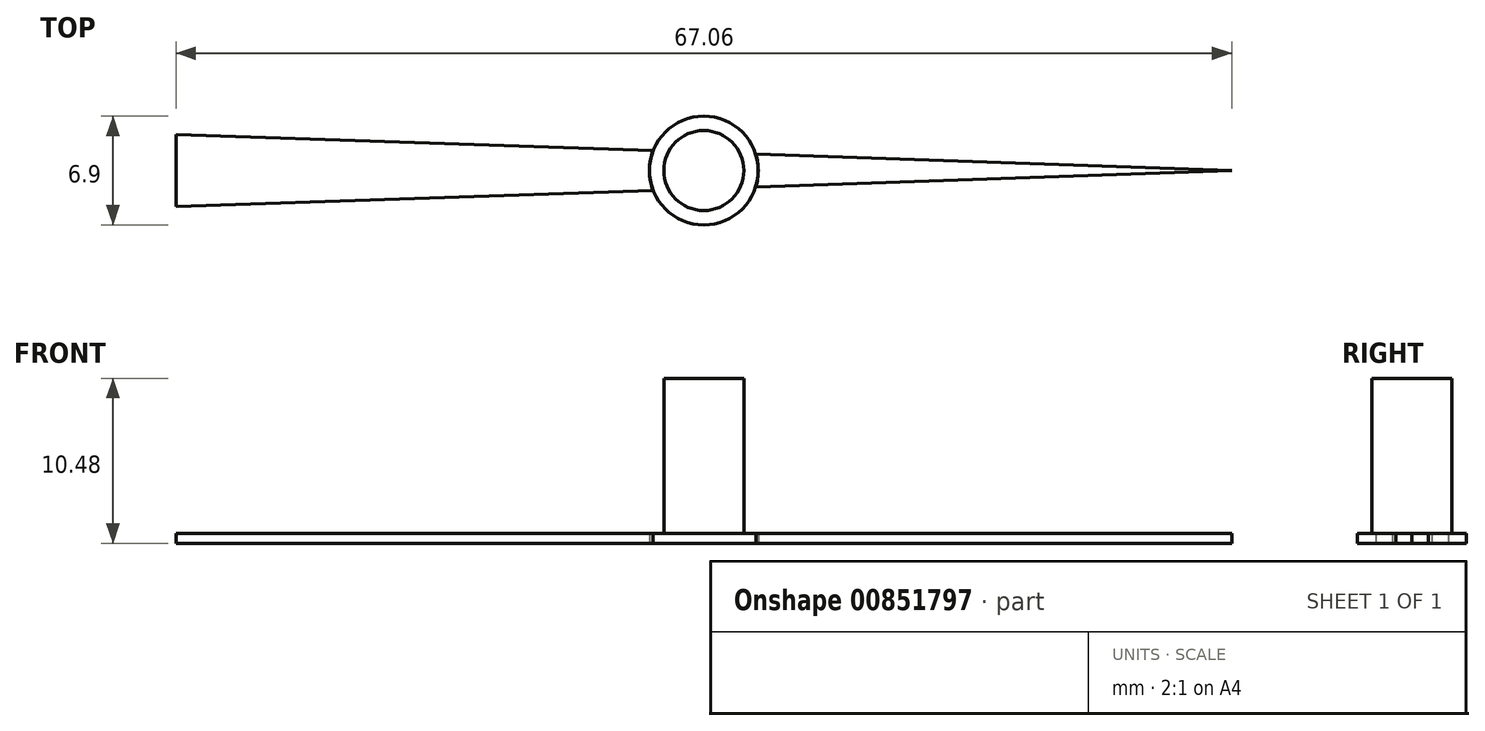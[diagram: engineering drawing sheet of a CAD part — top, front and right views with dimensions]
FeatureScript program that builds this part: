
annotation { "Feature Type Name" : "Feature", "Feature Type Description" : "" }
export const myFeature = defineFeature(function(context is Context, id is Id, definition is map)
    precondition{}
    {
        {
            var Q0;
            Q0=qCreatedBy(makeId("Top.planeOp"),FACE);
            var sketch = newSketch(context, id + "F0", { "sketchPlane" : qUnion([Q0])});
            skLineSegment(sketch, "E0.left", {"start": v(-33.53, 2.3) * mm, "end": v(-33.53, -2.3) * mm});
            skPoint(sketch, "E0.middle", {"position": v(0, 0) * mm});
            skPoint(sketch, "E1", {"position": v(33.53, 0) * mm});
            skLineSegment(sketch, "E2", {"start": v(33.53, 0) * mm, "end": v(-33.53, 2.3) * mm});
            skLineSegment(sketch, "E3", {"start": v(33.53, 0) * mm, "end": v(-33.53, -2.3) * mm});
            skCircle(sketch, "E4", {"center": v(0, 0) * mm, "radius": 3.45 * mm});
            skLineSegment(sketch, "E5.bottom", {"start": v(-2.67, 0.95) * mm, "end": v(2.67, 0.95) * mm});
            skLineSegment(sketch, "E5.top", {"start": v(-2.67, -0.95) * mm, "end": v(2.67, -0.95) * mm});
            skLineSegment(sketch, "E5.left", {"start": v(-2.67, 0.95) * mm, "end": v(-2.67, -0.95) * mm});
            skLineSegment(sketch, "E5.right", {"start": v(2.67, 0.95) * mm, "end": v(2.67, -0.95) * mm});
            skCircle(sketch, "E6", {"center": v(0, 0) * mm, "radius": 2.54 * mm});
            skCircle(sketch, "E7", {"center": v(0, 0) * mm, "radius": 3.46 * mm});
            skSolve(sketch);
        }
        {
            var Q0;
            {var subQ0=sQuery(id+"F0.wireOp",EDGE,"E0.left");Q0=makeQuery(id+"F0.imprint","IMPRINT",FACE,{"disambiguationData":[TD([[makeQuery(id+"F0.imprint","IMPRINT",EDGE,{"derivedFrom":subQ0}),1.0]])]});}
            var Q1;
            {var subQ0=sQuery(id+"F0.wireOp",EDGE,"E4");var subQ1=sQuery(id+"F0.wireOp",EDGE,"E3");var subQ2=makeQuery(id+"F0.imprint","INTERSECT",VERTEX,{"disambiguationData":[OD(0.0)],"derivedFrom":[subQ1,subQ0]});Q1=makeQuery(id+"F0.imprint","IMPRINT",FACE,{"disambiguationData":[TD([[makeQuery(id+"F0.imprint","IMPRINT",EDGE,{"disambiguationData":[TD([[subQ2,-1.0]])],"derivedFrom":subQ1}),1.0]])]});}
            var Q2;
            {var subQ0=sQuery(id+"F0.wireOp",EDGE,"E3");var subQ1=sQuery(id+"F0.wireOp",EDGE,"E2");var subQ2=makeQuery(id+"F0.imprint","INTERSECT",VERTEX,{"derivedFrom":[subQ1,subQ0]});Q2=makeQuery(id+"F0.imprint","IMPRINT",FACE,{"disambiguationData":[TD([[makeQuery(id+"F0.imprint","IMPRINT",EDGE,{"disambiguationData":[TD([[subQ2,-1.0]])],"derivedFrom":subQ1}),1.0]])]});}
            var Q3;
            {var subQ0=sQuery(id+"F0.wireOp",EDGE,"E4");var subQ1=sQuery(id+"F0.wireOp",EDGE,"E2");var subQ2=makeQuery(id+"F0.imprint","INTERSECT",VERTEX,{"disambiguationData":[OD(0.0)],"derivedFrom":[subQ1,subQ0]});Q3=makeQuery(id+"F0.imprint","IMPRINT",FACE,{"disambiguationData":[TD([[makeQuery(id+"F0.imprint","IMPRINT",EDGE,{"disambiguationData":[TD([[subQ2,-1.0]])],"derivedFrom":subQ1}),-1.0]])]});}
            var Q4;
            {var subQ0=sQuery(id+"F0.wireOp",EDGE,"E5.left");Q4=makeQuery(id+"F0.imprint","IMPRINT",FACE,{"disambiguationData":[TD([[makeQuery(id+"F0.imprint","IMPRINT",EDGE,{"derivedFrom":subQ0}),-1.0]])]});}
            var Q5;
            {var subQ5=sQuery(id+"F0.wireOp",EDGE,"E5.right");Q5=makeQuery(id+"F0.imprint","IMPRINT",FACE,{"disambiguationData":[TD([[makeQuery(id+"F0.imprint","IMPRINT",EDGE,{"derivedFrom":subQ5}),1.0]])]});}
            extrude(context, id + "F1", {"entities" : qUnion([Q0, Q1, Q2, Q3, Q4, Q5]), "endBound" : BoundingType.SYMMETRIC, "depth" : 0.64 * mm, "offsetDistance" : 25.4 * mm});
        }
        {
            var Q0;
            {var subQ0=sQuery(id+"F0.wireOp",EDGE,"E6");var subQ1=sQuery(id+"F0.wireOp",EDGE,"E3");var subQ2=makeQuery(id+"F0.imprint","INTERSECT",VERTEX,{"disambiguationData":[OD(0.0)],"derivedFrom":[subQ1,subQ0]});Q0=makeQuery(id+"F0.imprint","IMPRINT",FACE,{"disambiguationData":[TD([[makeQuery(id+"F0.imprint","IMPRINT",EDGE,{"disambiguationData":[TD([[subQ2,-1.0]])],"derivedFrom":subQ1}),1.0]])]});}
            var Q1;
            {var subQ0=sQuery(id+"F0.wireOp",EDGE,"E6");var subQ1=sQuery(id+"F0.wireOp",EDGE,"E2");var subQ2=makeQuery(id+"F0.imprint","INTERSECT",VERTEX,{"disambiguationData":[OD(0.0)],"derivedFrom":[subQ1,subQ0]});Q1=makeQuery(id+"F0.imprint","IMPRINT",FACE,{"disambiguationData":[TD([[makeQuery(id+"F0.imprint","IMPRINT",EDGE,{"disambiguationData":[TD([[subQ2,-1.0]])],"derivedFrom":subQ1}),-1.0]])]});}
            var Q2;
            {var subQ0=sQuery(id+"F0.wireOp",EDGE,"E6");var subQ1=sQuery(id+"F0.wireOp",EDGE,"E5.bottom");var subQ2=makeQuery(id+"F0.imprint","INTERSECT",VERTEX,{"disambiguationData":[OD(0.0)],"derivedFrom":[subQ1,subQ0]});Q2=makeQuery(id+"F0.imprint","IMPRINT",FACE,{"disambiguationData":[TD([[makeQuery(id+"F0.imprint","IMPRINT",EDGE,{"disambiguationData":[TD([[subQ2,-1.0]])],"derivedFrom":subQ1}),-1.0]])]});}
            var Q3;
            {var subQ0=sQuery(id+"F0.wireOp",EDGE,"E6");var subQ1=sQuery(id+"F0.wireOp",EDGE,"E2");var subQ2=makeQuery(id+"F0.imprint","INTERSECT",VERTEX,{"disambiguationData":[OD(0.0)],"derivedFrom":[subQ1,subQ0]});Q3=makeQuery(id+"F0.imprint","IMPRINT",FACE,{"disambiguationData":[TD([[makeQuery(id+"F0.imprint","IMPRINT",EDGE,{"disambiguationData":[TD([[subQ2,-1.0]])],"derivedFrom":subQ1}),1.0]])]});}
            var Q4;
            {var subQ0=sQuery(id+"F0.wireOp",EDGE,"E6");var subQ1=sQuery(id+"F0.wireOp",EDGE,"E3");var subQ2=makeQuery(id+"F0.imprint","INTERSECT",VERTEX,{"disambiguationData":[OD(0.0)],"derivedFrom":[subQ1,subQ0]});Q4=makeQuery(id+"F0.imprint","IMPRINT",FACE,{"disambiguationData":[TD([[makeQuery(id+"F0.imprint","IMPRINT",EDGE,{"disambiguationData":[TD([[subQ2,-1.0]])],"derivedFrom":subQ1}),-1.0]])]});}
            extrude(context, id + "F2", {"entities" : qUnion([Q0, Q1, Q2, Q3, Q4]), "operationType" : NewBodyOperationType.ADD, "depth" : 10.16 * mm, "offsetDistance" : 25.4 * mm});
        }
        {
            var Q0;
            {var subQ0=sQuery(id+"F0.wireOp",EDGE,"E6");var subQ1=sQuery(id+"F0.wireOp",EDGE,"E3");var subQ2=makeQuery(id+"F0.imprint","INTERSECT",VERTEX,{"disambiguationData":[OD(0.0)],"derivedFrom":[subQ1,subQ0]});Q0=makeQuery(id+"F0.imprint","IMPRINT",FACE,{"disambiguationData":[TD([[makeQuery(id+"F0.imprint","IMPRINT",EDGE,{"disambiguationData":[TD([[subQ2,-1.0]])],"derivedFrom":subQ1}),1.0]])]});}
            var Q1;
            {var subQ0=sQuery(id+"F0.wireOp",EDGE,"E6");var subQ1=sQuery(id+"F0.wireOp",EDGE,"E5.bottom");var subQ2=makeQuery(id+"F0.imprint","INTERSECT",VERTEX,{"disambiguationData":[OD(0.0)],"derivedFrom":[subQ1,subQ0]});Q1=makeQuery(id+"F0.imprint","IMPRINT",FACE,{"disambiguationData":[TD([[makeQuery(id+"F0.imprint","IMPRINT",EDGE,{"disambiguationData":[TD([[subQ2,-1.0]])],"derivedFrom":subQ1}),-1.0]])]});}
            var Q2;
            {var subQ0=sQuery(id+"F0.wireOp",EDGE,"E6");var subQ1=sQuery(id+"F0.wireOp",EDGE,"E2");var subQ2=makeQuery(id+"F0.imprint","INTERSECT",VERTEX,{"disambiguationData":[OD(0.0)],"derivedFrom":[subQ1,subQ0]});Q2=makeQuery(id+"F0.imprint","IMPRINT",FACE,{"disambiguationData":[TD([[makeQuery(id+"F0.imprint","IMPRINT",EDGE,{"disambiguationData":[TD([[subQ2,-1.0]])],"derivedFrom":subQ1}),-1.0]])]});}
            var Q3;
            {var subQ0=sQuery(id+"F0.wireOp",EDGE,"E6");var subQ1=sQuery(id+"F0.wireOp",EDGE,"E3");var subQ2=makeQuery(id+"F0.imprint","INTERSECT",VERTEX,{"disambiguationData":[OD(0.0)],"derivedFrom":[subQ1,subQ0]});Q3=makeQuery(id+"F0.imprint","IMPRINT",FACE,{"disambiguationData":[TD([[makeQuery(id+"F0.imprint","IMPRINT",EDGE,{"disambiguationData":[TD([[subQ2,-1.0]])],"derivedFrom":subQ1}),-1.0]])]});}
            var Q4;
            {var subQ0=sQuery(id+"F0.wireOp",EDGE,"E5.left");Q4=makeQuery(id+"F0.imprint","IMPRINT",FACE,{"disambiguationData":[TD([[makeQuery(id+"F0.imprint","IMPRINT",EDGE,{"derivedFrom":subQ0}),1.0]])]});}
            var Q5;
            {var subQ0=sQuery(id+"F0.wireOp",EDGE,"E6");var subQ1=sQuery(id+"F0.wireOp",EDGE,"E2");var subQ2=makeQuery(id+"F0.imprint","INTERSECT",VERTEX,{"disambiguationData":[OD(0.0)],"derivedFrom":[subQ1,subQ0]});Q5=makeQuery(id+"F0.imprint","IMPRINT",FACE,{"disambiguationData":[TD([[makeQuery(id+"F0.imprint","IMPRINT",EDGE,{"disambiguationData":[TD([[subQ2,-1.0]])],"derivedFrom":subQ1}),1.0]])]});}
            var Q6;
            {var subQ0=sQuery(id+"F0.wireOp",EDGE,"E5.right");Q6=makeQuery(id+"F0.imprint","IMPRINT",FACE,{"disambiguationData":[TD([[makeQuery(id+"F0.imprint","IMPRINT",EDGE,{"derivedFrom":subQ0}),-1.0]])]});}
            extrude(context, id + "F3", {"entities" : qUnion([Q0, Q1, Q2, Q3, Q4, Q5, Q6]), "operationType" : NewBodyOperationType.ADD, "endBound" : BoundingType.SYMMETRIC, "oppositeDirection" : true, "depth" : 0.64 * mm, "offsetDistance" : 25.4 * mm});
        }
    });
